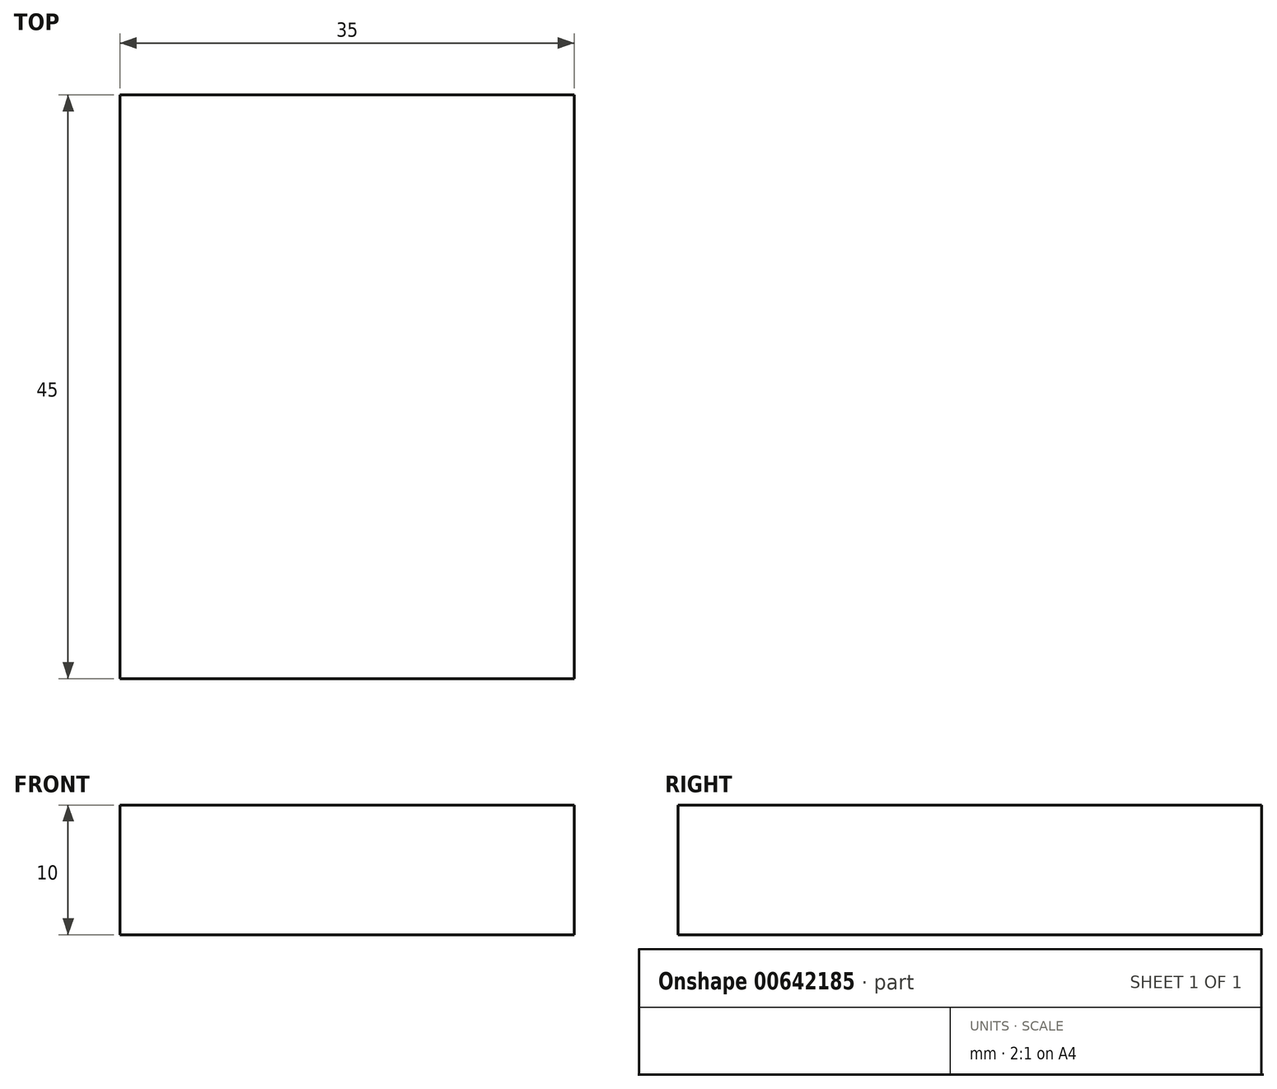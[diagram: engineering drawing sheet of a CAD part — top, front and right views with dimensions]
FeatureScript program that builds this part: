
annotation { "Feature Type Name" : "Feature", "Feature Type Description" : "" }
export const myFeature = defineFeature(function(context is Context, id is Id, definition is map)
    precondition{}
    {
        {
            var Q0;
            Q0=qCreatedBy(makeId("Top.planeOp"),FACE);
            var sketch = newSketch(context, id + "F0", { "sketchPlane" : qUnion([Q0])});
            skLineSegment(sketch, "E0.bottom", {"start": v(17.5, -22.5) * mm, "end": v(-17.5, -22.5) * mm});
            skLineSegment(sketch, "E0.top", {"start": v(17.5, 22.5) * mm, "end": v(-17.5, 22.5) * mm});
            skLineSegment(sketch, "E0.left", {"start": v(17.5, -22.5) * mm, "end": v(17.5, 22.5) * mm});
            skLineSegment(sketch, "E0.right", {"start": v(-17.5, -22.5) * mm, "end": v(-17.5, 22.5) * mm});
            skPoint(sketch, "E0.middle", {"position": v(0, 0) * mm});
            skSolve(sketch);
        }
        {
            var Q0;
            Q0 = qSketchRegion(id + "F0", true);
            extrude(context, id + "F1", {"entities" : qUnion([Q0]), "oppositeDirection" : true, "depth" : 10 * mm, "offsetDistance" : 25.4 * mm});
        }
    });
